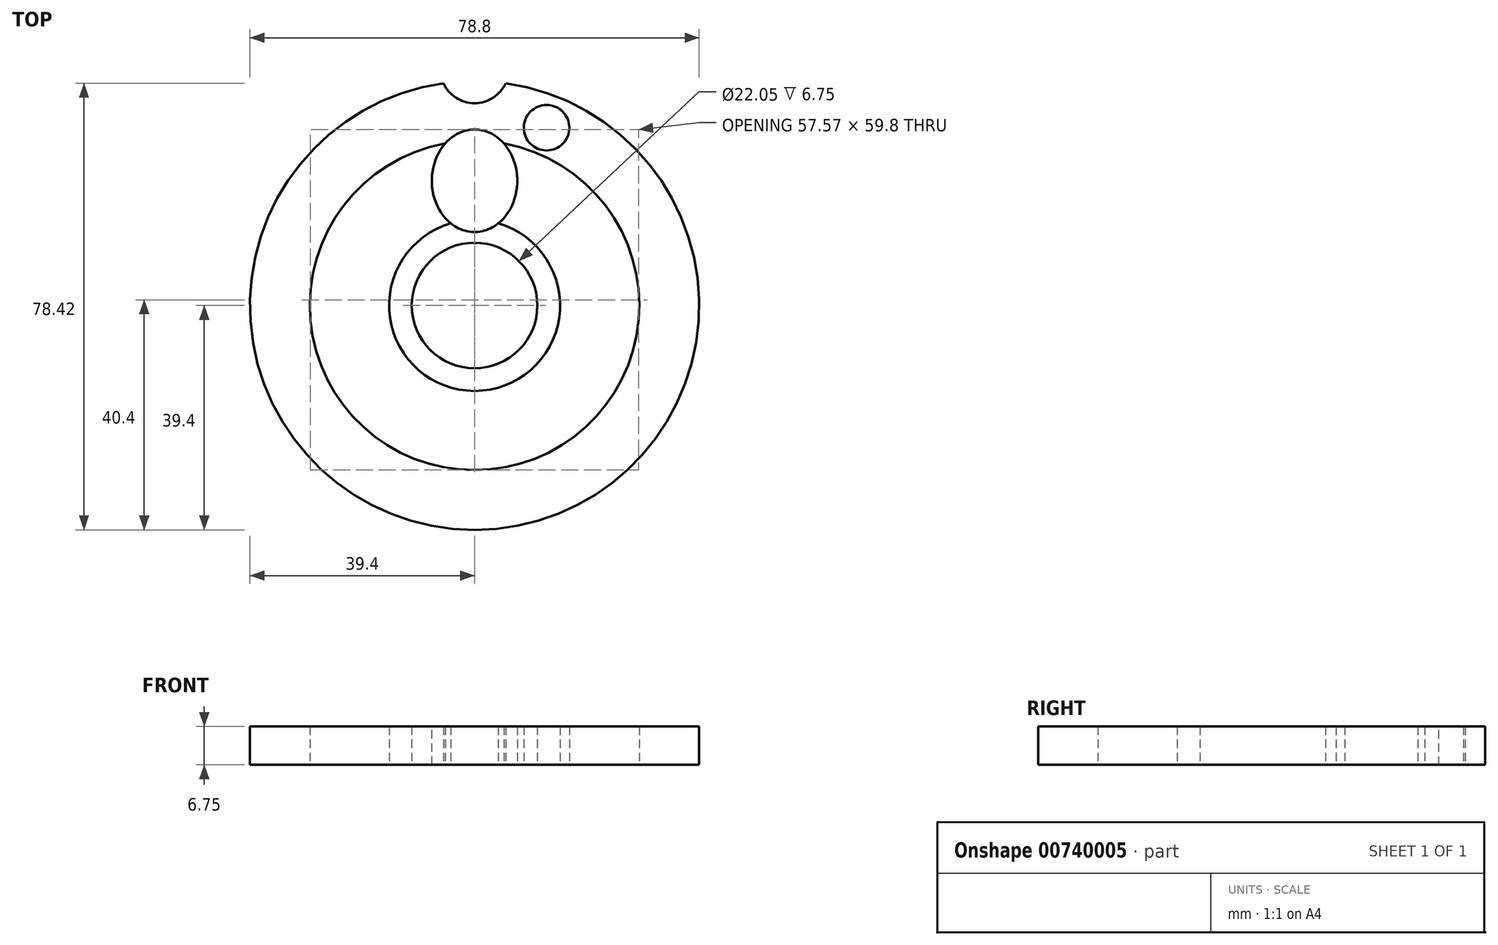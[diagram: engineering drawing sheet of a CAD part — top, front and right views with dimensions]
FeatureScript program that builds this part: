
annotation { "Feature Type Name" : "Feature", "Feature Type Description" : "" }
export const myFeature = defineFeature(function(context is Context, id is Id, definition is map)
    precondition{}
    {
        {
            var Q0;
            Q0=qCreatedBy(makeId("Top.planeOp"),FACE);
            var sketch = newSketch(context, id + "F0", { "sketchPlane" : qUnion([Q0])});
            skCircle(sketch, "E0", {"center": v(0, 0) * mm, "radius": 11.03 * mm});
            skCircle(sketch, "E1", {"center": v(0, 0) * mm, "radius": 39.4 * mm});
            skCircle(sketch, "E2.0", {"center": v(0, 0) * mm, "radius": 28.9 * mm});
            skCircle(sketch, "E3", {"center": v(0, 0) * mm, "radius": 15 * mm});
            skPoint(sketch, "E4.0.midPoint", {"position": v(3.5, 16.62) * mm});
            skSolve(sketch);
        }
        {
            var Q0;
            Q0=makeQuery(id+"F0.imprint","IMPRINT",FACE,{"disambiguationData":[TD([[makeQuery(id+"F0.imprint","IMPRINT",EDGE,{"derivedFrom":sQuery(id+"F0.wireOp",EDGE,"E2.0")}),1.0]])]});
            var sketch = newSketch(context, id + "F1", { "sketchPlane" : qUnion([Q0])});
            skCircle(sketch, "E5", {"center": v(0, 41.52) * mm, "radius": 6 * mm});
            skSolve(sketch);
        }
        {
            var Q0;
            Q0=makeQuery(id+"F0.imprint","IMPRINT",FACE,{"disambiguationData":[TD([[makeQuery(id+"F0.imprint","IMPRINT",EDGE,{"derivedFrom":sQuery(id+"F0.wireOp",EDGE,"E1")}),1.0]])]});
            var Q1;
            Q1=makeQuery(id+"F1.imprint","IMPRINT",FACE,{"disambiguationData":[TD([[makeQuery(id+"F1.imprint","IMPRINT",EDGE,{"derivedFrom":makeQuery(id+"F0.imprint","IMPRINT",EDGE,{"derivedFrom":sQuery(id+"F0.wireOp",EDGE,"E2.0")})}),1.0]])]});
            var Q2;
            Q2=makeQuery(id+"F0.imprint","IMPRINT",FACE,{"disambiguationData":[TD([[makeQuery(id+"F0.imprint","IMPRINT",EDGE,{"derivedFrom":sQuery(id+"F0.wireOp",EDGE,"E0")}),-1.0]])]});
            extrude(context, id + "F2", {"entities" : qUnion([Q0, Q1, Q2]), "depth" : 6.75 * mm, "offsetDistance" : 25 * mm});
        }
        {
            var Q0;
            Q0 = qSketchRegion(id + "F1", true);
            extrude(context, id + "F3", {"entities" : qUnion([Q0]), "operationType" : NewBodyOperationType.REMOVE, "depth" : 10.6 * mm, "offsetDistance" : 25 * mm});
        }
        {
            var Q0;
            Q0=qCreatedBy(makeId("Top.planeOp"),FACE);
            var sketch = newSketch(context, id + "F4", { "sketchPlane" : qUnion([Q0])});
            skCircle(sketch, "E6", {"center": v(12.64, 31.2) * mm, "radius": 4 * mm});
            skSolve(sketch);
        }
        {
            var Q0;
            Q0 = qSketchRegion(id + "F4", true);
            extrude(context, id + "F5", {"entities" : qUnion([Q0]), "operationType" : NewBodyOperationType.REMOVE, "depth" : 15 * mm, "offsetDistance" : 25 * mm});
        }
        {
            var Q0;
            Q0=qCreatedBy(makeId("Top.planeOp"),FACE);
            var sketch = newSketch(context, id + "F6", { "sketchPlane" : qUnion([Q0])});
            skEllipse(sketch, "E7", {"center": v(0, 21.9) * mm, "majorRadius": 9 * mm, "minorRadius": 7.5 * mm, "majorAxis": v(0, -1)});
            skSolve(sketch);
        }
        {
            var Q0;
            Q0 = qSketchRegion(id + "F6", true);
            extrude(context, id + "F7", {"entities" : qUnion([Q0]), "operationType" : NewBodyOperationType.REMOVE, "depth" : 10.6 * mm, "offsetDistance" : 25 * mm});
        }
    });
